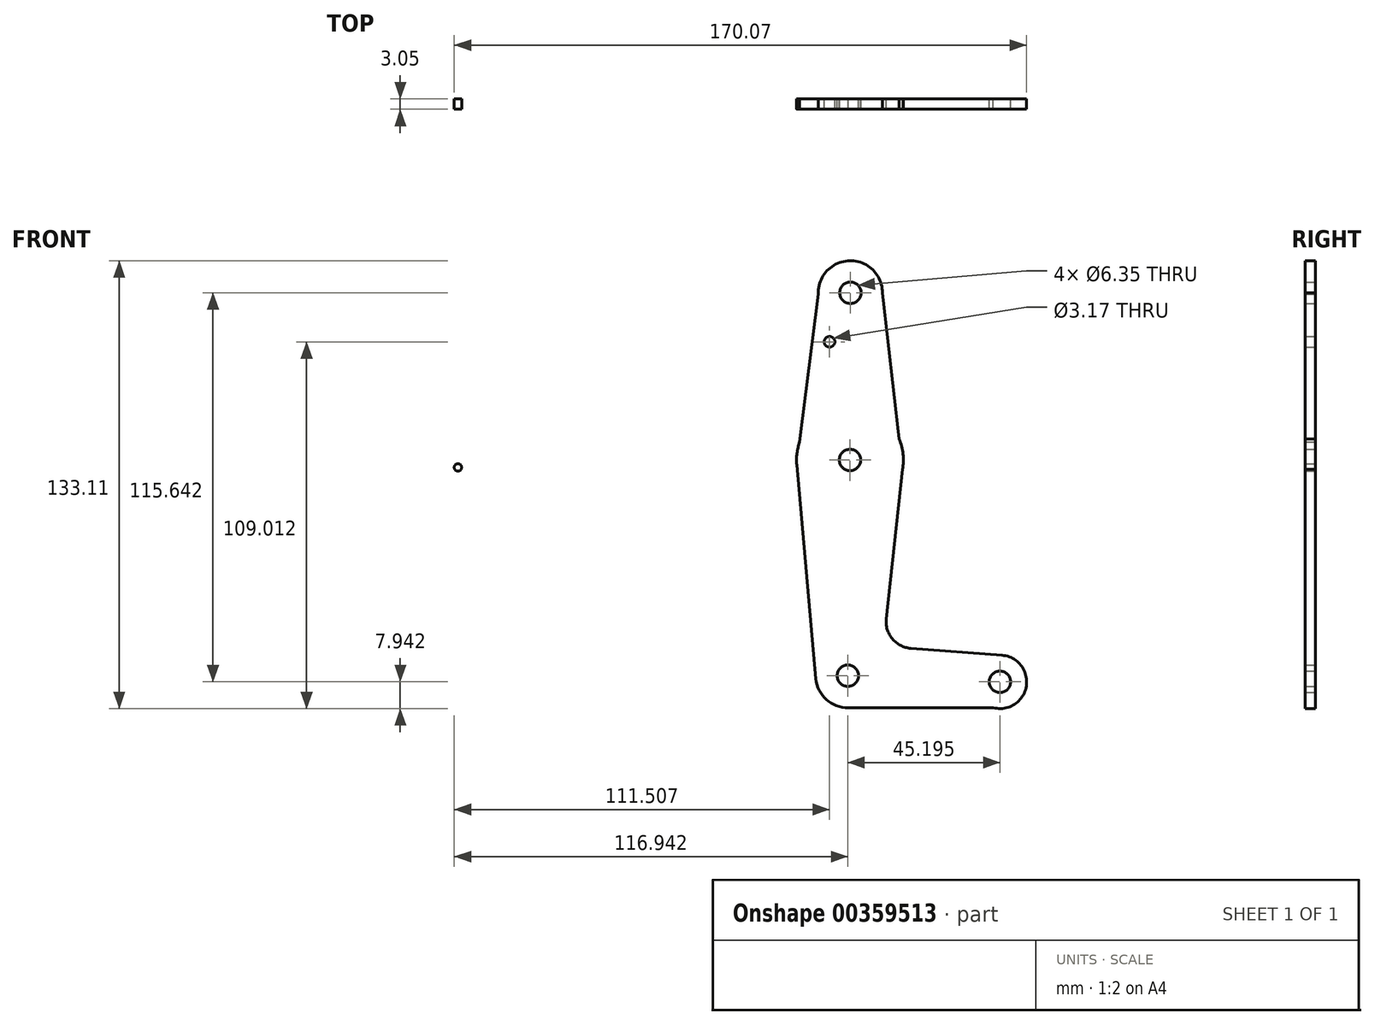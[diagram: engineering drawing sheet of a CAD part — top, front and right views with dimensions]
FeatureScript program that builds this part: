
annotation { "Feature Type Name" : "Feature", "Feature Type Description" : "" }
export const myFeature = defineFeature(function(context is Context, id is Id, definition is map)
    precondition{}
    {
        {
            var Q0;
            Q0=qCreatedBy(makeId("Front.planeOp"),FACE);
            var sketch = newSketch(context, id + "F0", { "sketchPlane" : qUnion([Q0])});
            skCircle(sketch, "E0", {"center": v(-33.97, 49.7) * mm, "radius": 9.53 * mm});
            skCircle(sketch, "E1", {"center": v(-34.1, 0) * mm, "radius": 15.88 * mm});
            skCircle(sketch, "E2", {"center": v(-34.74, -64.1) * mm, "radius": 9.53 * mm});
            skCircle(sketch, "E3", {"center": v(-150.57, -2.2) * mm, "radius": 1.1 * mm});
            skCircle(sketch, "E4", {"center": v(10.46, -65.94) * mm, "radius": 7.94 * mm});
            skLineSegment(sketch, "E5", {"start": v(-34, -15.87) * mm, "end": v(-34, -54.61) * mm});
            skLineSegment(sketch, "E6", {"start": v(-49.9, -1.45) * mm, "end": v(-44.23, -64.95) * mm});
            skLineSegment(sketch, "E7", {"start": v(-18.47, -2.83) * mm, "end": v(-23.31, -47.18) * mm});
            skLineSegment(sketch, "E8", {"start": v(-43.5, 49.35) * mm, "end": v(-49.9, -1.45) * mm});
            skLineSegment(sketch, "E9", {"start": v(-34.32, 15.87) * mm, "end": v(-34.32, 40.19) * mm});
            skLineSegment(sketch, "E10", {"start": v(-24.45, 49.7) * mm, "end": v(-18.47, -2.83) * mm});
            skLineSegment(sketch, "E11", {"start": v(-34.57, -73.63) * mm, "end": v(12.42, -73.63) * mm});
            skLineSegment(sketch, "E12", {"start": v(-16, -55.97) * mm, "end": v(12.42, -58.13) * mm});
            skLineSegment(sketch, "E13", {"start": v(-34.74, -64.1) * mm, "end": v(10.46, -65.94) * mm});
            skCircle(sketch, "E14", {"center": v(-33.97, 49.7) * mm, "radius": 3.18 * mm});
            skCircle(sketch, "E15", {"center": v(-34.1, 0) * mm, "radius": 3.18 * mm});
            skCircle(sketch, "E16", {"center": v(-34.74, -64.1) * mm, "radius": 3.18 * mm});
            skCircle(sketch, "E17", {"center": v(10.46, -65.94) * mm, "radius": 3.18 * mm});
            skCircle(sketch, "E18", {"center": v(-40.17, 35.13) * mm, "radius": 1.59 * mm});
            skArc(sketch, "E19.filletArc", {"start": v(-23.31, -47.18) * mm, "mid": v(-21.52, -53.13) * mm, "end": v(-16, -55.97) * mm});
            skSolve(sketch);
        }
        {
            var Q0;
            Q0 = qSketchRegion(id + "F0", true);
            extrude(context, id + "F1", {"entities" : qUnion([Q0]), "depth" : 3.05 * mm});
        }
    });
